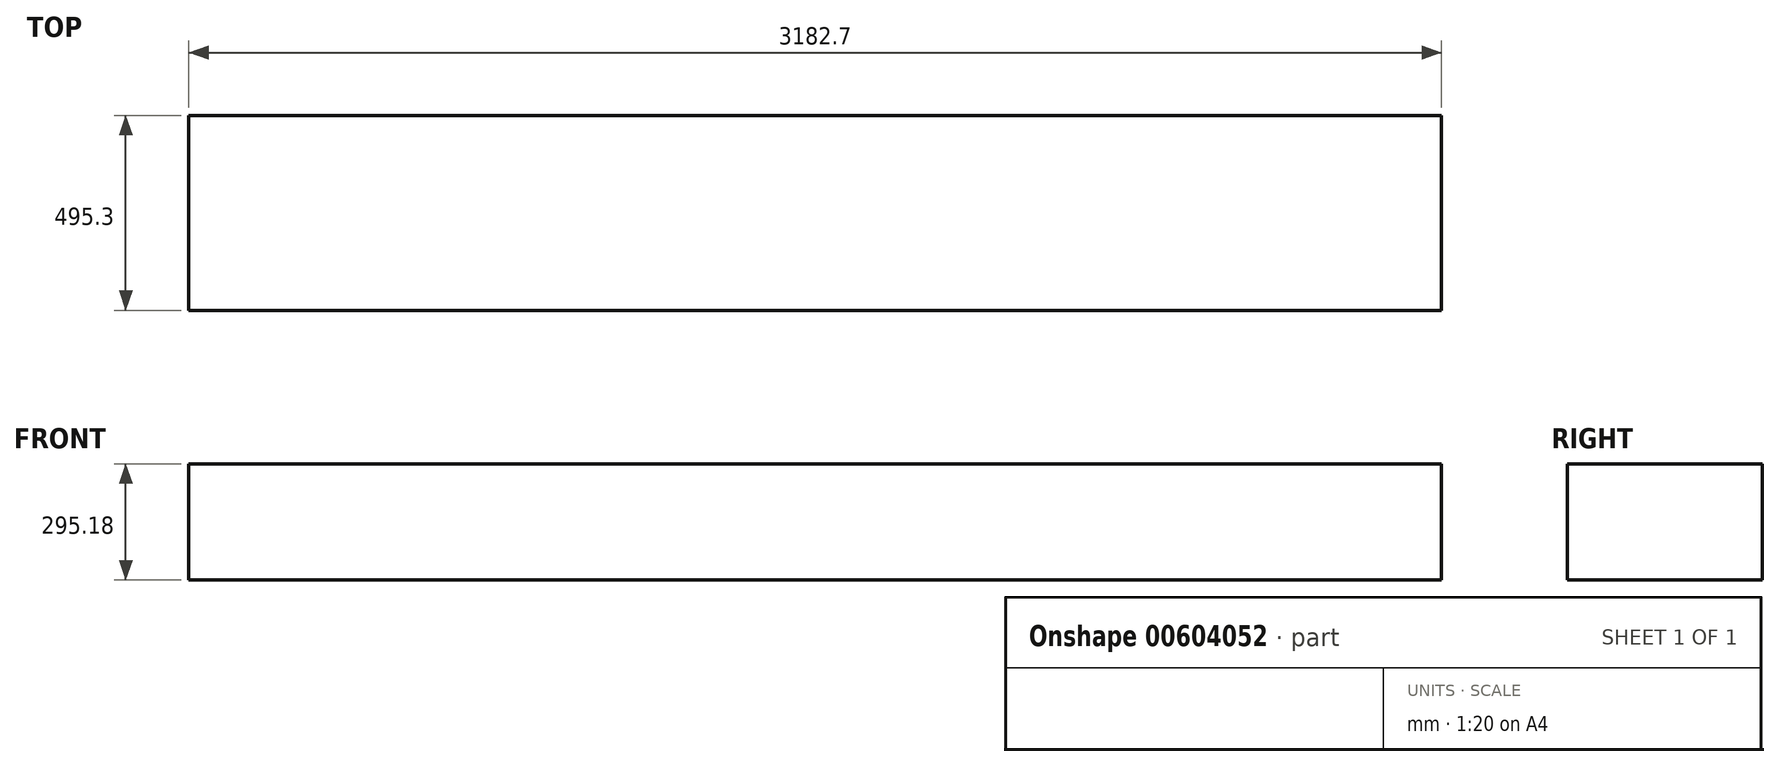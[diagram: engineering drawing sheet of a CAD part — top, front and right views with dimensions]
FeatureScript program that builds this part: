
annotation { "Feature Type Name" : "Feature", "Feature Type Description" : "" }
export const myFeature = defineFeature(function(context is Context, id is Id, definition is map)
    precondition{}
    {
        {
            var Q0;
            Q0=qCreatedBy(makeId("Front.planeOp"),FACE);
            var sketch = newSketch(context, id + "F0", { "sketchPlane" : qUnion([Q0])});
            skLineSegment(sketch, "E0.bottom", {"start": v(-494.79, 115.12) * mm, "end": v(2687.9, 115.12) * mm});
            skLineSegment(sketch, "E0.top", {"start": v(-494.79, -180.06) * mm, "end": v(2687.9, -180.06) * mm});
            skLineSegment(sketch, "E0.left", {"start": v(-494.79, 115.12) * mm, "end": v(-494.79, -180.06) * mm});
            skLineSegment(sketch, "E0.right", {"start": v(2687.9, 115.12) * mm, "end": v(2687.9, -180.06) * mm});
            skSolve(sketch);
        }
        {
            var Q0;
            Q0 = qSketchRegion(id + "F0", true);
            extrude(context, id + "F1", {"entities" : qUnion([Q0]), "depth" : 203.2 * mm, "offsetDistance" : 25.4 * mm, "hasSecondDirection" : true, "secondDirectionOppositeDirection" : true, "secondDirectionDepth" : 292.1 * mm});
        }
    });
